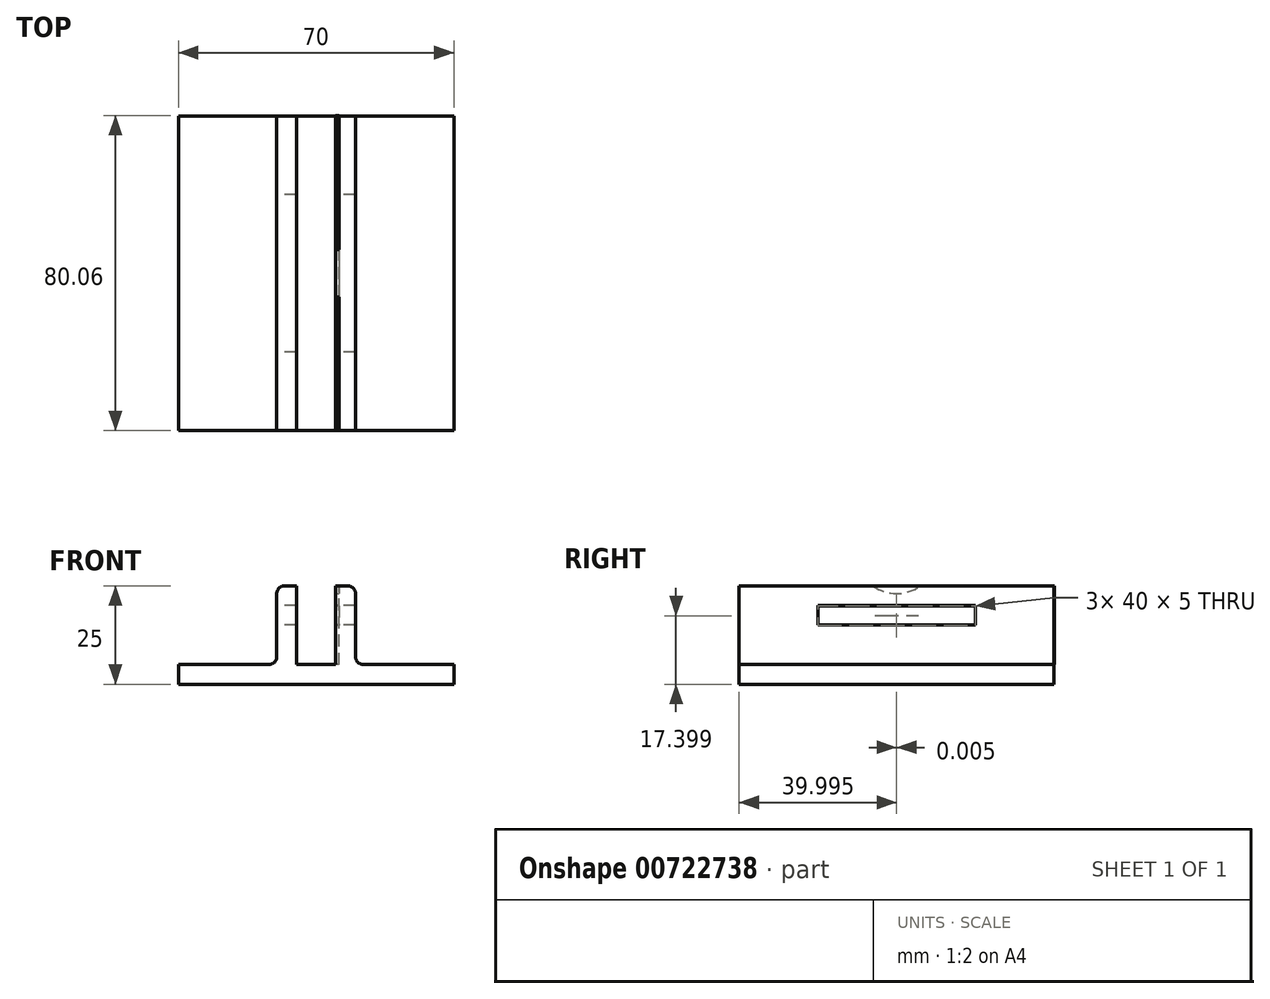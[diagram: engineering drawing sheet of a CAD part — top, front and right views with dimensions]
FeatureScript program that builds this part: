
annotation { "Feature Type Name" : "Feature", "Feature Type Description" : "" }
export const myFeature = defineFeature(function(context is Context, id is Id, definition is map)
    precondition{}
    {
        {
            var Q0;
            Q0=qCreatedBy(makeId("Front.planeOp"),FACE);
            var sketch = newSketch(context, id + "F0", { "sketchPlane" : qUnion([Q0])});
            skLineSegment(sketch, "E0.bottom", {"start": v(0, 0) * mm, "end": v(-10, 0) * mm, "construction": true});
            skLineSegment(sketch, "E0.top", {"start": v(0, 20) * mm, "end": v(-10, 20) * mm, "construction": true});
            skLineSegment(sketch, "E0.left", {"start": v(0, 0) * mm, "end": v(0, 20) * mm, "construction": true});
            skLineSegment(sketch, "E0.right", {"start": v(-10, 0) * mm, "end": v(-10, 20) * mm, "construction": true});
            skLineSegment(sketch, "E1.bottom", {"start": v(-10, 20) * mm, "end": v(-15, 20) * mm});
            skLineSegment(sketch, "E1.top", {"start": v(-10, 0) * mm, "end": v(-15, 0) * mm, "construction": true});
            skLineSegment(sketch, "E1.left", {"start": v(-10, 20) * mm, "end": v(-10, 0) * mm});
            skLineSegment(sketch, "E1.right", {"start": v(-15, 20) * mm, "end": v(-15, 0) * mm});
            skLineSegment(sketch, "E2.bottom", {"start": v(0, 20) * mm, "end": v(5, 20) * mm});
            skLineSegment(sketch, "E2.top", {"start": v(0, 0) * mm, "end": v(5, 0) * mm});
            skLineSegment(sketch, "E2.left", {"start": v(0, 20) * mm, "end": v(0, 0) * mm});
            skLineSegment(sketch, "E2.right", {"start": v(5, 20) * mm, "end": v(5, 0) * mm});
            skLineSegment(sketch, "E3.bottom", {"start": v(0, 0) * mm, "end": v(-40, 0) * mm});
            skLineSegment(sketch, "E3.top", {"start": v(0, -5) * mm, "end": v(-40, -5) * mm});
            skLineSegment(sketch, "E3.left", {"start": v(0, 0) * mm, "end": v(0, -5) * mm});
            skLineSegment(sketch, "E3.right", {"start": v(-40, 0) * mm, "end": v(-40, -5) * mm});
            skLineSegment(sketch, "E4.bottom", {"start": v(0, 0) * mm, "end": v(30, 0) * mm});
            skLineSegment(sketch, "E4.top", {"start": v(0, -5) * mm, "end": v(30, -5) * mm});
            skLineSegment(sketch, "E4.right", {"start": v(30, 0) * mm, "end": v(30, -5) * mm});
            skSolve(sketch);
        }
        {
            var Q0;
            Q0=qSketchRegion(id+"F0",true);
            extrude(context, id + "F1", {"entities" : qUnion([Q0]), "depth" : 80 * mm, "offsetDistance" : 25 * mm, "symmetric" : true});
        }
        {
            var Q0;
            Q0=makeQuery(id+"F1.opExtrude","SWEPT_EDGE",EDGE,{"disambiguationData":[OSD([sQuery(id+"F0.wireOp",EDGE,"E2.right"),sQuery(id+"F0.wireOp",EDGE,"E4.bottom")])]});
            var Q1;
            Q1=makeQuery(id+"F1.opExtrude","SWEPT_EDGE",EDGE,{"disambiguationData":[OSD([sQuery(id+"F0.wireOp",EDGE,"E1.right"),sQuery(id+"F0.wireOp",EDGE,"E3.bottom")])]});
            fillet(context, id + "F2", {"entities" : qUnion([Q0, Q1]), "radius" : 2 * mm, "tangentPropagation" : true, "allowEdgeOverflow" : false});
        }
        {
            var Q0;
            Q0=makeQuery(id+"F1.opExtrude","SWEPT_EDGE",EDGE,{"disambiguationData":[OSD([sQuery(id+"F0.wireOp",EDGE,"E1.bottom"),sQuery(id+"F0.wireOp",EDGE,"E1.right")])]});
            var Q1;
            Q1=makeQuery(id+"F1.opExtrude","SWEPT_EDGE",EDGE,{"disambiguationData":[OSD([sQuery(id+"F0.wireOp",EDGE,"E2.bottom"),sQuery(id+"F0.wireOp",EDGE,"E2.right")])]});
            fillet(context, id + "F3", {"entities" : qUnion([Q0, Q1]), "radius" : 2 * mm, "tangentPropagation" : true, "allowEdgeOverflow" : false});
        }
        {
            var Q0;
            Q0=makeQuery(id+"F1.opExtrude","SWEPT_FACE",FACE,{"disambiguationData":[OSD([sQuery(id+"F0.wireOp",EDGE,"E1.right")])]});
            var sketch = newSketch(context, id + "F4", { "sketchPlane" : qUnion([Q0])});
            skLineSegment(sketch, "E5", {"start": v(-40, 0) * mm, "end": v(-20, 0) * mm, "construction": true});
            skLineSegment(sketch, "E6", {"start": v(-20, 0) * mm, "end": v(-20, 10) * mm, "construction": true});
            skLineSegment(sketch, "E7.bottom", {"start": v(-20, 10) * mm, "end": v(20, 10) * mm});
            skLineSegment(sketch, "E7.top", {"start": v(-20, 15) * mm, "end": v(20, 15) * mm});
            skLineSegment(sketch, "E7.left", {"start": v(-20, 10) * mm, "end": v(-20, 15) * mm});
            skLineSegment(sketch, "E7.right", {"start": v(20, 10) * mm, "end": v(20, 15) * mm});
            skSolve(sketch);
        }
        {
            var Q0;
            Q0=qSketchRegion(id+"F4",true);
            extrude(context, id + "F5", {"entities" : qUnion([Q0]), "operationType" : NewBodyOperationType.REMOVE, "oppositeDirection" : true, "depth" : 25 * mm, "offsetDistance" : 25 * mm});
        }
        {
            var Q0;
            Q0=makeQuery(id+"F1.opExtrude","SWEPT_FACE",FACE,{"disambiguationData":[OSD([sQuery(id+"F0.wireOp",EDGE,"E2.right")])]});
            var sketch = newSketch(context, id + "F6", { "sketchPlane" : qUnion([Q0])});
            skLineSegment(sketch, "E8", {"start": v(0, 0) * mm, "end": v(0, 28) * mm, "construction": true});
            skCircle(sketch, "E9", {"center": v(0, 28) * mm, "radius": 10 * mm});
            skSolve(sketch);
        }
        {
            var Q0;
            Q0=qSketchRegion(id+"F6",true);
            extrude(context, id + "F7", {"entities" : qUnion([Q0]), "oppositeDirection" : true, "depth" : 25 * mm, "offsetDistance" : 25 * mm});
        }
        {
            var Q0;
            Q0=qCreatedBy(makeId("Right.planeOp"),FACE);
            var sketch = newSketch(context, id + "F8", { "sketchPlane" : qUnion([Q0])});
            skLineSegment(sketch, "E10.bottom", {"start": v(40.06, 0) * mm, "end": v(-39.94, 0) * mm});
            skLineSegment(sketch, "E10.top", {"start": v(40.06, 20) * mm, "end": v(-39.94, 20) * mm});
            skLineSegment(sketch, "E10.left", {"start": v(40.06, 0) * mm, "end": v(40.06, 20) * mm});
            skLineSegment(sketch, "E10.right", {"start": v(-39.94, 0) * mm, "end": v(-39.94, 20) * mm});
            skLineSegment(sketch, "E11.bottom", {"start": v(20, 14.9) * mm, "end": v(-20, 14.9) * mm});
            skLineSegment(sketch, "E11.top", {"start": v(20, 9.9) * mm, "end": v(-20, 9.9) * mm});
            skLineSegment(sketch, "E11.left", {"start": v(20, 14.9) * mm, "end": v(20, 9.9) * mm});
            skLineSegment(sketch, "E11.right", {"start": v(-20, 14.9) * mm, "end": v(-20, 9.9) * mm});
            skSolve(sketch);
        }
        {
            var Q0;
            Q0 = qSketchRegion(id + "F8", true);
            extrude(context, id + "F9", {"entities" : qUnion([Q0]), "depth" : 0.8 * mm, "offsetDistance" : 25 * mm});
        }
        {
            var Q0;
            Q0=makeQuery(id+"F7.opExtrude","SWEPT_BODY",BODY,{"disambiguationData":[OSD([sQuery(id+"F6.wireOp",EDGE,"E9")])]});
            var Q1;
            Q1=makeQuery(id+"F9.opExtrude","SWEPT_BODY",BODY,{"disambiguationData":[OSD([sQuery(id+"F8.wireOp",EDGE,"E10.bottom"),sQuery(id+"F8.wireOp",EDGE,"E10.top"),sQuery(id+"F8.wireOp",EDGE,"E10.left"),sQuery(id+"F8.wireOp",EDGE,"E10.right"),sQuery(id+"F8.wireOp",EDGE,"E11.bottom"),sQuery(id+"F8.wireOp",EDGE,"E11.top"),sQuery(id+"F8.wireOp",EDGE,"E11.left"),sQuery(id+"F8.wireOp",EDGE,"E11.right")])]});
            booleanBodies(context, id + "F10", {"operationType" : BooleanOperationType.SUBTRACTION, "tools" : qUnion([Q0]), "targets" : qUnion([Q1])});
        }
    });
